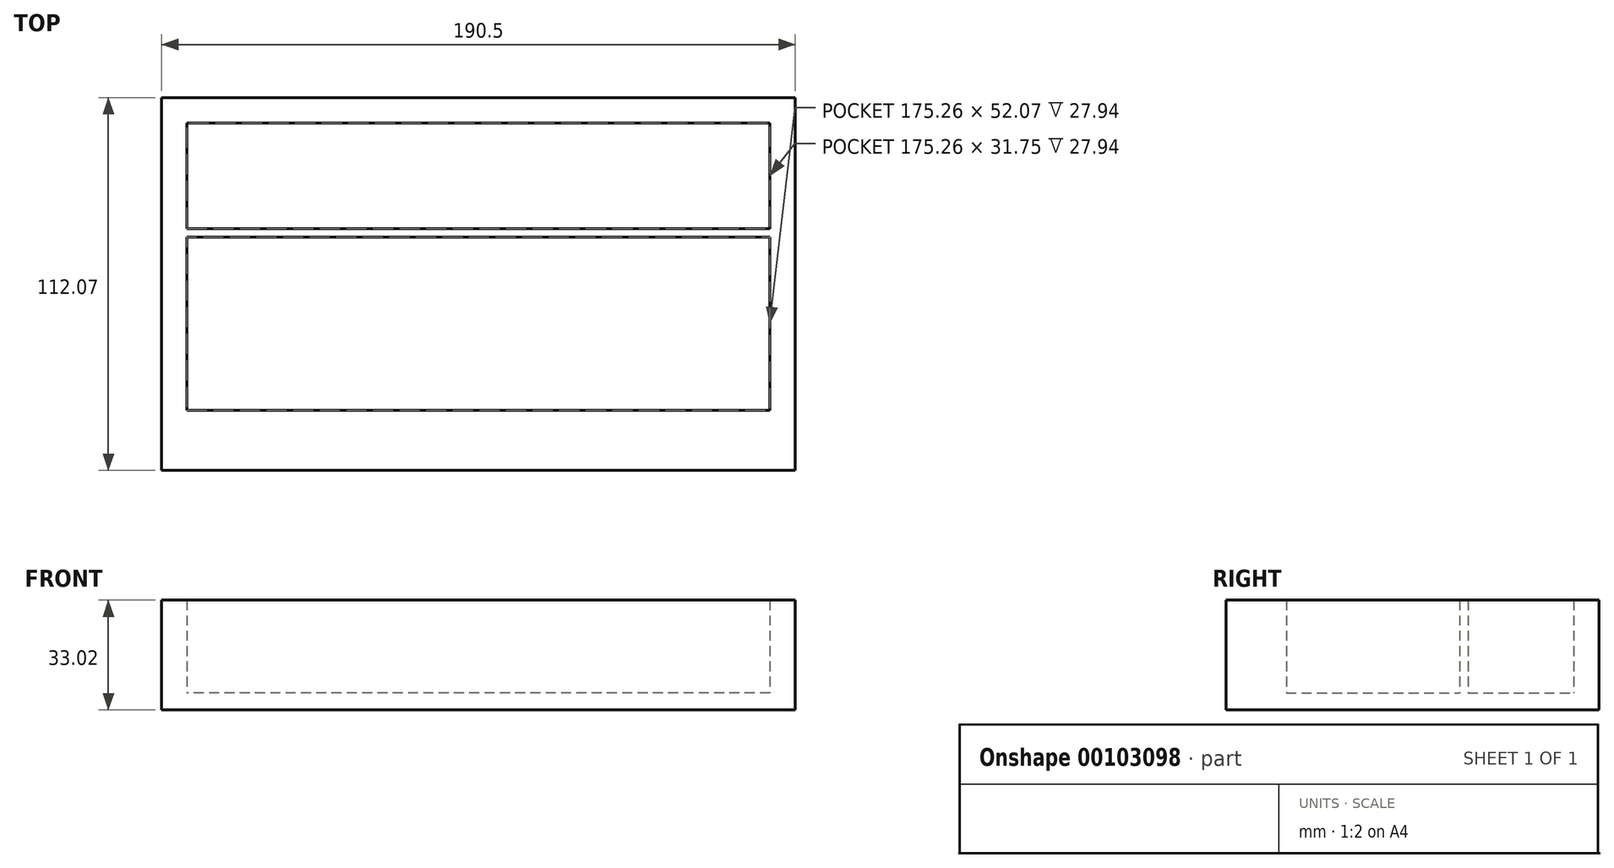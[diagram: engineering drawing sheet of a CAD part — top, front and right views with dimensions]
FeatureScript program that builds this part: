
annotation { "Feature Type Name" : "Feature", "Feature Type Description" : "" }
export const myFeature = defineFeature(function(context is Context, id is Id, definition is map)
    precondition{}
    {
        {
            var Q0;
            Q0=qCreatedBy(makeId("Top.planeOp"),FACE);
            var sketch = newSketch(context, id + "F0", { "sketchPlane" : qUnion([Q0])});
            skLineSegment(sketch, "E0", {"start": v(-95.25, 0) * mm, "end": v(95.25, 0) * mm});
            skLineSegment(sketch, "E1", {"start": v(-95.25, 0) * mm, "end": v(-95.25, 101.6) * mm});
            skLineSegment(sketch, "E2", {"start": v(-95.25, 101.6) * mm, "end": v(95.25, 101.6) * mm});
            skLineSegment(sketch, "E3", {"start": v(95.25, 101.6) * mm, "end": v(95.25, 0) * mm});
            skLineSegment(sketch, "E4.0", {"start": v(-87.63, 7.62) * mm, "end": v(87.63, 7.62) * mm});
            skLineSegment(sketch, "E4.1", {"start": v(-87.63, 7.62) * mm, "end": v(-87.63, 93.98) * mm});
            skLineSegment(sketch, "E4.2", {"start": v(-87.63, 93.98) * mm, "end": v(87.63, 93.98) * mm});
            skLineSegment(sketch, "E4.3", {"start": v(87.63, 93.98) * mm, "end": v(87.63, 7.62) * mm});
            skLineSegment(sketch, "E5", {"start": v(87.63, 62.23) * mm, "end": v(-87.63, 62.23) * mm});
            skLineSegment(sketch, "E6.0", {"start": v(87.63, 59.7) * mm, "end": v(-87.63, 59.69) * mm});
            skSolve(sketch);
        }
        {
            var Q0;
            Q0=makeQuery(id+"F0.imprint","IMPRINT",FACE,{"disambiguationData":[TD([[makeQuery(id+"F0.imprint","IMPRINT",EDGE,{"derivedFrom":sQuery(id+"F0.wireOp",EDGE,"E0")}),1.0]])]});
            var Q1;
            {var subQ0=sQuery(id+"F0.wireOp",EDGE,"E5");Q1=makeQuery(id+"F0.imprint","IMPRINT",FACE,{"disambiguationData":[TD([[makeQuery(id+"F0.imprint","IMPRINT",EDGE,{"derivedFrom":subQ0}),1.0]])]});}
            extrude(context, id + "F1", {"entities" : qUnion([Q0, Q1]), "depth" : 33.02 * mm});
        }
        {
            var Q0;
            {var subQ0=sQuery(id+"F0.wireOp",EDGE,"E4.2");Q0=makeQuery(id+"F0.imprint","IMPRINT",FACE,{"disambiguationData":[TD([[makeQuery(id+"F0.imprint","IMPRINT",EDGE,{"derivedFrom":subQ0}),-1.0]])]});}
            var Q1;
            {var subQ0=sQuery(id+"F0.wireOp",EDGE,"E4.0");Q1=makeQuery(id+"F0.imprint","IMPRINT",FACE,{"disambiguationData":[TD([[makeQuery(id+"F0.imprint","IMPRINT",EDGE,{"derivedFrom":subQ0}),1.0]])]});}
            extrude(context, id + "F2", {"entities" : qUnion([Q0, Q1]), "operationType" : NewBodyOperationType.ADD, "depth" : 5.08 * mm});
        }
        {
            var Q0;
            Q0=makeQuery(id+"F1.opExtrude","CAP_FACE",FACE,{"disambiguationData":[OSD([sQuery(id+"F0.wireOp",EDGE,"E0"),sQuery(id+"F0.wireOp",EDGE,"E1"),sQuery(id+"F0.wireOp",EDGE,"E2"),sQuery(id+"F0.wireOp",EDGE,"E3"),sQuery(id+"F0.wireOp",EDGE,"E4.0"),sQuery(id+"F0.wireOp",EDGE,"E4.1"),sQuery(id+"F0.wireOp",EDGE,"E4.2"),sQuery(id+"F0.wireOp",EDGE,"E4.3"),sQuery(id+"F0.wireOp",EDGE,"E5"),sQuery(id+"F0.wireOp",EDGE,"E6.0")])],"isStart":false});
            var sketch = newSketch(context, id + "F3", { "sketchPlane" : qUnion([Q0])});
            skLineSegment(sketch, "E7", {"start": v(-95.25, 0) * mm, "end": v(-95.25, -10.47) * mm});
            skLineSegment(sketch, "E8", {"start": v(95.25, 0) * mm, "end": v(95.25, -10.47) * mm});
            skLineSegment(sketch, "E9", {"start": v(95.25, -10.47) * mm, "end": v(-95.25, -10.47) * mm});
            skPoint(sketch, "E10", {"position": v(0, -10.47) * mm});
            skSolve(sketch);
        }
        {
            var Q0;
            Q0=makeQuery(id+"F3.imprint","IMPRINT",FACE,{"disambiguationData":[TD([[makeQuery(id+"F3.imprint","IMPRINT",EDGE,{"derivedFrom":sQuery(id+"F3.wireOp",EDGE,"E7")}),1.0]])]});
            extrude(context, id + "F4", {"entities" : qUnion([Q0]), "operationType" : NewBodyOperationType.ADD, "oppositeDirection" : true, "depth" : 33.02 * mm});
        }
    });
